# Revit family: Lockers_Series-50_Lincora
name_source: partatom
category: Casework
units: mm (PartAtom-declared; Revit-internal decimal feet)

## family parameters
Always vertical = Yes
Cut with Voids When Loaded = No
Room Calculation Point = No
Shared = No
Work Plane-Based = No

## types (12) — shared parameters
CAD Details = https://www.arcat.com
Default Elevation = 0"
Depth = 28"
Height = 90"
Hook Material = Aluminum
Hook Width = 46"
Keynote = 10 51 00
Lock Material = Aluminum
Manufacturer = Lincora
Max Depth = 28"
Max Height = 90"
Max Width = 48"
Min Depth = 12"
Min Height = 30 1/2"
Min Width = 9"
Model = Series 50
Number Plate Material = Black Plastic
Product Page URL = https://www.arcat.com
Requested Depth = 28"
Requested Height = 90"
Requested Width = 48"
Specification = https://www.arcat.com
URL = https://www.lincora.com
Width = 48"

## per-type parameters (varying)
| type | Base Material | Body Material | Door Material | Increment |
| Series 50_White | White | White | White | 8-Jan |
| Series 50_Nevada Beige | Nevada Beige | Nevada Beige | Nevada Beige |  |
| Series 50_Pearl Gray | Pearl Gray | Pearl Gray | Pearl Gray |  |
| Series 50_Aluminum Gray | Aluminum Gray | Aluminum Gray | Aluminum Gray |  |
| Series 50_Platinum Gray | Platinum Gray | Platinum Gray | Platinum Gray |  |
| Series 50_Medium Gray | Medium Gray | Medium Gray | Medium Gray |  |
| Series 50_Dark Gray | Dark Gray | Dark Gray | Dark Gray |  |
| Series 50_Ocean Blue | Ocean Blue | Ocean Blue | Ocean Blue |  |
| Series 50_Azure Blue | Azure Blue | Azure Blue | Azure Blue |  |
| Series 50_Dark Blue | Dark Blue | Dark Blue | Dark Blue |  |
| Series 50_Black | Black | Black | Black |  |
| Series 50_Red | Red | Red | Red |  |

## geometry (parser evidence)
native form markers: Sweep x7
no freeform markers — native parametric forms only
